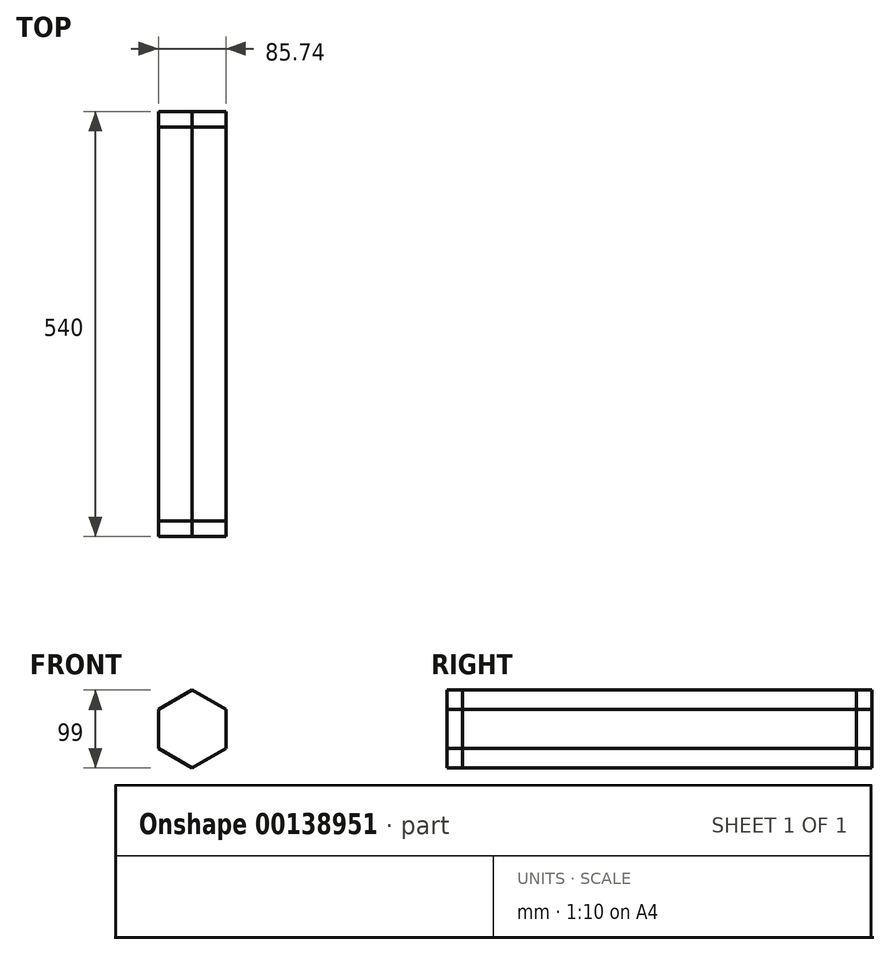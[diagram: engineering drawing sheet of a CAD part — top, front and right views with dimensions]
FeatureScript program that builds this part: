
annotation { "Feature Type Name" : "Feature", "Feature Type Description" : "" }
export const myFeature = defineFeature(function(context is Context, id is Id, definition is map)
    precondition{}
    {
        {
            var Q0;
            Q0=qCreatedBy(makeId("Front.planeOp"),FACE);
            var sketch = newSketch(context, id + "F0", { "sketchPlane" : qUnion([Q0])});
            skCircle(sketch, "E0.cCircle", {"center": v(0, 0) * mm, "radius": 42.87 * mm, "construction": true});
            skLineSegment(sketch, "E0.0", {"start": v(-42.87, -24.75) * mm, "end": v(-42.87, 24.75) * mm});
            skLineSegment(sketch, "E0.1", {"start": v(-42.87, 24.75) * mm, "end": v(0, 49.5) * mm});
            skLineSegment(sketch, "E0.2", {"start": v(0, 49.5) * mm, "end": v(42.87, 24.75) * mm});
            skLineSegment(sketch, "E0.3", {"start": v(42.87, 24.75) * mm, "end": v(42.87, -24.75) * mm});
            skLineSegment(sketch, "E0.4", {"start": v(42.87, -24.75) * mm, "end": v(0, -49.5) * mm});
            skLineSegment(sketch, "E0.5", {"start": v(0, -49.5) * mm, "end": v(-42.87, -24.75) * mm});
            skPoint(sketch, "E0.0.midPoint", {"position": v(-42.87, 0) * mm});
            skSolve(sketch);
        }
        {
            var Q0;
            Q0 = qSketchRegion(id + "F0", true);
            var Q1;
            Q1=makeQuery(id+"F0.imprint","IMPRINT",FACE,{"disambiguationData":[TD([[makeQuery(id+"F0.imprint","IMPRINT",EDGE,{"derivedFrom":sQuery(id+"F0.wireOp",EDGE,"E0.0")}),-1.0]])]});
            extrude(context, id + "F1", {"entities" : qUnion([Q0, Q1]), "depth" : 500 * mm});
        }
        {
            var Q0;
            Q0=makeQuery(id+"F1.opExtrude","SWEPT_FACE",FACE,{"disambiguationData":[OSD([sQuery(id+"F0.wireOp",EDGE,"E0.3")])]});
            var sketch = newSketch(context, id + "F2", { "sketchPlane" : qUnion([Q0])});
            skLineSegment(sketch, "E1", {"start": v(-350, 24.75) * mm, "end": v(-401.77, -24.75) * mm});
            skLineSegment(sketch, "E2", {"start": v(-401.77, -24.75) * mm, "end": v(-500, -24.75) * mm});
            skSolve(sketch);
        }
        {
            var Q0;
            Q0=makeQuery(id+"F1.opExtrude","SWEPT_FACE",FACE,{"disambiguationData":[OSD([sQuery(id+"F0.wireOp",EDGE,"E0.4")])]});
            var sketch = newSketch(context, id + "F3", { "sketchPlane" : qUnion([Q0])});
            skLineSegment(sketch, "E3", {"start": v(24.75, 400) * mm, "end": v(-24.75, 350) * mm});
            skSolve(sketch);
        }
        {
            var Q0;
            Q0=makeQuery(id+"F1.opExtrude","SWEPT_FACE",FACE,{"disambiguationData":[OSD([sQuery(id+"F0.wireOp",EDGE,"E0.1")])]});
            var sketch = newSketch(context, id + "F4", { "sketchPlane" : qUnion([Q0])});
            skLineSegment(sketch, "E4", {"start": v(24.75, -350) * mm, "end": v(-24.75, -400) * mm});
            skSolve(sketch);
        }
        {
            var Q0;
            Q0=makeQuery(id+"F1.opExtrude","SWEPT_FACE",FACE,{"disambiguationData":[OSD([sQuery(id+"F0.wireOp",EDGE,"E0.0")])]});
            var sketch = newSketch(context, id + "F5", { "sketchPlane" : qUnion([Q0])});
            skLineSegment(sketch, "E5", {"start": v(350, -24.75) * mm, "end": v(400, 24.75) * mm});
            skSolve(sketch);
        }
        {
            var Q0;
            Q0=makeQuery(id+"F1.opExtrude","CAP_FACE",FACE,{"disambiguationData":[OSD([sQuery(id+"F0.wireOp",EDGE,"E0.0"),sQuery(id+"F0.wireOp",EDGE,"E0.1"),sQuery(id+"F0.wireOp",EDGE,"E0.2"),sQuery(id+"F0.wireOp",EDGE,"E0.3"),sQuery(id+"F0.wireOp",EDGE,"E0.4"),sQuery(id+"F0.wireOp",EDGE,"E0.5")])],"isStart":false});
            extrude(context, id + "F6", {"entities" : qUnion([Q0]), "depth" : 20 * mm});
        }
        {
            var Q0;
            Q0=makeQuery(id+"F1.opExtrude","CAP_FACE",FACE,{"disambiguationData":[OSD([sQuery(id+"F0.wireOp",EDGE,"E0.0"),sQuery(id+"F0.wireOp",EDGE,"E0.1"),sQuery(id+"F0.wireOp",EDGE,"E0.2"),sQuery(id+"F0.wireOp",EDGE,"E0.3"),sQuery(id+"F0.wireOp",EDGE,"E0.4"),sQuery(id+"F0.wireOp",EDGE,"E0.5")])],"isStart":true});
            extrude(context, id + "F7", {"entities" : qUnion([Q0]), "depth" : 20 * mm});
        }
    });
